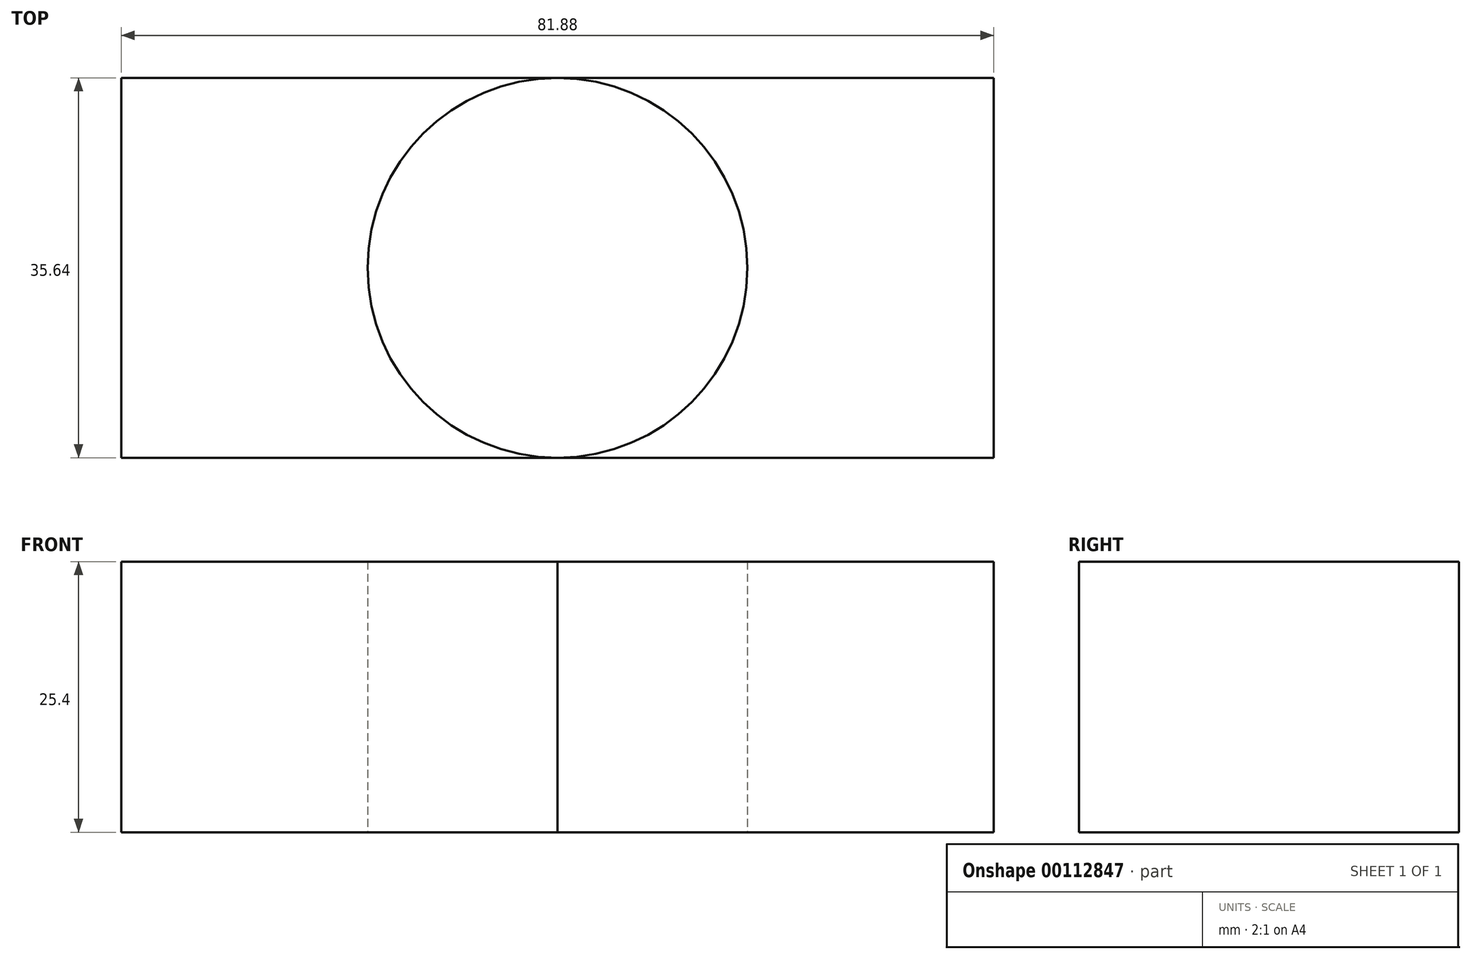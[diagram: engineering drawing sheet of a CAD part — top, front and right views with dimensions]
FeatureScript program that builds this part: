
annotation { "Feature Type Name" : "Feature", "Feature Type Description" : "" }
export const myFeature = defineFeature(function(context is Context, id is Id, definition is map)
    precondition{}
    {
        {
            var Q0;
            Q0=qCreatedBy(makeId("Top.planeOp"),FACE);
            var sketch = newSketch(context, id + "F0", { "sketchPlane" : qUnion([Q0])});
            skLineSegment(sketch, "E0.bottom", {"start": v(40.94, -17.82) * mm, "end": v(-40.94, -17.82) * mm});
            skLineSegment(sketch, "E0.top", {"start": v(40.94, 17.82) * mm, "end": v(-40.94, 17.82) * mm});
            skLineSegment(sketch, "E0.left", {"start": v(40.94, -17.82) * mm, "end": v(40.94, 17.82) * mm});
            skLineSegment(sketch, "E0.right", {"start": v(-40.94, -17.82) * mm, "end": v(-40.94, 17.82) * mm});
            skPoint(sketch, "E0.middle", {"position": v(0, 0) * mm});
            skCircle(sketch, "E1", {"center": v(0, 0) * mm, "radius": 17.82 * mm});
            skSolve(sketch);
        }
        {
            var Q0;
            {var subQ0=sQuery(id+"F0.wireOp",EDGE,"E0.left");Q0=makeQuery(id+"F0.imprint","IMPRINT",FACE,{"disambiguationData":[TD([[makeQuery(id+"F0.imprint","IMPRINT",EDGE,{"derivedFrom":subQ0}),1.0]])]});}
            var Q1;
            {var subQ0=sQuery(id+"F0.wireOp",EDGE,"E0.right");Q1=makeQuery(id+"F0.imprint","IMPRINT",FACE,{"disambiguationData":[TD([[makeQuery(id+"F0.imprint","IMPRINT",EDGE,{"derivedFrom":subQ0}),-1.0]])]});}
            extrude(context, id + "F1", {"entities" : qUnion([Q0, Q1]), "depth" : 25.4 * mm});
        }
    });
